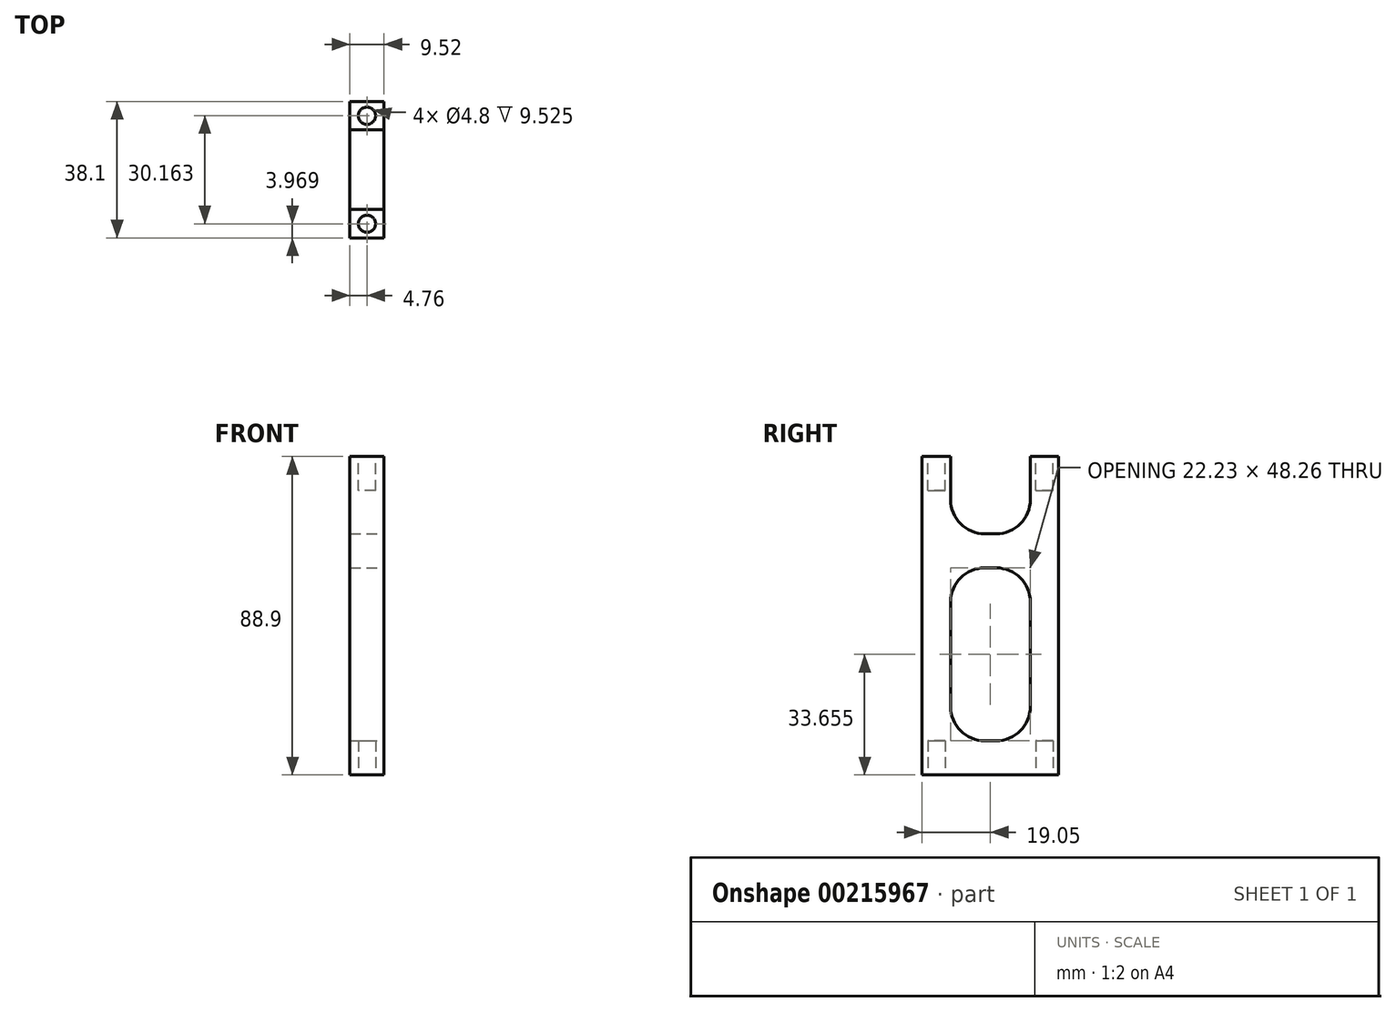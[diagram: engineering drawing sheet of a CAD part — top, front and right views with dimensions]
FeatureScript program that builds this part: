
annotation { "Feature Type Name" : "Feature", "Feature Type Description" : "" }
export const myFeature = defineFeature(function(context is Context, id is Id, definition is map)
    precondition{}
    {
        {
            var Q0;
            Q0=qCreatedBy(makeId("Right.planeOp"),FACE);
            var sketch = newSketch(context, id + "F0", { "sketchPlane" : qUnion([Q0])});
            skLineSegment(sketch, "E0.bottom", {"start": v(0, 0) * mm, "end": v(38.1, 0) * mm});
            skLineSegment(sketch, "E0.top", {"start": v(0, 88.9) * mm, "end": v(38.1, 88.9) * mm});
            skLineSegment(sketch, "E0.left", {"start": v(0, 0) * mm, "end": v(0, 88.9) * mm});
            skLineSegment(sketch, "E0.right", {"start": v(38.1, 0) * mm, "end": v(38.1, 88.9) * mm});
            skSolve(sketch);
        }
        {
            var Q0;
            Q0=qSketchRegion(id+"F0",true);
            extrude(context, id + "F1", {"entities" : qUnion([Q0]), "depth" : 9.52 * mm, "symmetric" : true});
        }
        {
            var Q0;
            Q0=makeQuery(id+"F1.opExtrude","CAP_FACE",FACE,{"disambiguationData":[OSD([sQuery(id+"F0.wireOp",EDGE,"E0.bottom"),sQuery(id+"F0.wireOp",EDGE,"E0.top"),sQuery(id+"F0.wireOp",EDGE,"E0.left"),sQuery(id+"F0.wireOp",EDGE,"E0.right")])],"isStart":false});
            var sketch = newSketch(context, id + "F2", { "sketchPlane" : qUnion([Q0])});
            skLineSegment(sketch, "E1", {"start": v(19.05, 0) * mm, "end": v(19.05, 117.7) * mm, "construction": true});
            skLineSegment(sketch, "E2", {"start": v(7.94, 88.9) * mm, "end": v(30.16, 88.9) * mm});
            skPoint(sketch, "E3", {"position": v(19.05, 88.9) * mm});
            skLineSegment(sketch, "E4", {"start": v(7.94, 88.9) * mm, "end": v(7.94, 76.84) * mm});
            skLineSegment(sketch, "E5", {"start": v(17.46, 67.31) * mm, "end": v(20.64, 67.31) * mm});
            skLineSegment(sketch, "E6", {"start": v(30.16, 88.9) * mm, "end": v(30.16, 76.84) * mm});
            skPoint(sketch, "E7.visualSharp", {"position": v(7.94, 67.31) * mm});
            skArc(sketch, "E7.filletArc", {"start": v(7.94, 76.84) * mm, "mid": v(10.73, 70.1) * mm, "end": v(17.46, 67.31) * mm});
            skPoint(sketch, "E8.visualSharp", {"position": v(30.16, 67.31) * mm});
            skArc(sketch, "E8.filletArc", {"start": v(20.64, 67.31) * mm, "mid": v(27.37, 70.1) * mm, "end": v(30.16, 76.84) * mm});
            skSolve(sketch);
        }
        {
            var Q0;
            Q0=qSketchRegion(id+"F2",true);
            extrude(context, id + "F3", {"entities" : qUnion([Q0]), "operationType" : NewBodyOperationType.REMOVE, "oppositeDirection" : true, "depth" : 25.4 * mm, "symmetric" : true});
        }
        {
            var Q0;
            {var subQ1=sQuery(id+"F0.wireOp",EDGE,"E0.left");var subQ2=sQuery(id+"F0.wireOp",EDGE,"E0.top");Q0=makeQuery(id+"F3.boolean.opBoolean","SPLIT",FACE,{"disambiguationData":[TD([makeQuery(id+"F1.opExtrude","SWEPT_FACE",FACE,{"disambiguationData":[OSD([subQ1])]})])],"derivedFrom":makeQuery(id+"F1.opExtrude","SWEPT_FACE",FACE,{"disambiguationData":[OSD([subQ2])]})});}
            var sketch = newSketch(context, id + "F4", { "sketchPlane" : qUnion([Q0])});
            skCircle(sketch, "E9", {"center": v(0, 3.97) * mm, "radius": 2.4 * mm});
            skCircle(sketch, "E10", {"center": v(0, 34.13) * mm, "radius": 2.4 * mm});
            skSolve(sketch);
        }
        {
            var Q0;
            Q0=qSketchRegion(id+"F4",true);
            extrude(context, id + "F5", {"entities" : qUnion([Q0]), "operationType" : NewBodyOperationType.REMOVE, "oppositeDirection" : true, "depth" : 9.52 * mm});
        }
        {
            var Q0;
            Q0=makeQuery(id+"F1.opExtrude","SWEPT_FACE",FACE,{"disambiguationData":[OSD([sQuery(id+"F0.wireOp",EDGE,"E0.bottom")])]});
            var sketch = newSketch(context, id + "F6", { "sketchPlane" : qUnion([Q0])});
            skCircle(sketch, "E11.0", {"center": v(0, -3.97) * mm, "radius": 2.4 * mm});
            skCircle(sketch, "E12.0", {"center": v(0, -34.13) * mm, "radius": 2.4 * mm});
            skSolve(sketch);
        }
        {
            var Q0;
            Q0=qSketchRegion(id+"F6",true);
            extrude(context, id + "F7", {"entities" : qUnion([Q0]), "operationType" : NewBodyOperationType.REMOVE, "oppositeDirection" : true, "depth" : 9.52 * mm});
        }
        {
            var Q0;
            Q0=makeQuery(id+"F1.opExtrude","CAP_FACE",FACE,{"disambiguationData":[OSD([sQuery(id+"F0.wireOp",EDGE,"E0.bottom"),sQuery(id+"F0.wireOp",EDGE,"E0.top"),sQuery(id+"F0.wireOp",EDGE,"E0.left"),sQuery(id+"F0.wireOp",EDGE,"E0.right")])],"isStart":false});
            var sketch = newSketch(context, id + "F8", { "sketchPlane" : qUnion([Q0])});
            skLineSegment(sketch, "E13", {"start": v(7.94, 76.84) * mm, "end": v(7.94, 0) * mm, "construction": true});
            skLineSegment(sketch, "E14", {"start": v(30.16, 76.84) * mm, "end": v(30.16, 0) * mm, "construction": true});
            skLineSegment(sketch, "E15.bottom", {"start": v(7.94, 57.79) * mm, "end": v(30.16, 57.79) * mm});
            skLineSegment(sketch, "E15.top", {"start": v(7.94, 9.53) * mm, "end": v(30.16, 9.53) * mm});
            skLineSegment(sketch, "E15.left", {"start": v(7.94, 57.79) * mm, "end": v(7.94, 9.52) * mm});
            skLineSegment(sketch, "E15.right", {"start": v(30.16, 57.79) * mm, "end": v(30.16, 9.52) * mm});
            skSolve(sketch);
        }
        {
            var Q0;
            Q0=qSketchRegion(id+"F8",true);
            extrude(context, id + "F9", {"entities" : qUnion([Q0]), "operationType" : NewBodyOperationType.REMOVE, "endBound" : BoundingType.THROUGH_ALL, "oppositeDirection" : true, "depth" : 25.4 * mm});
        }
        {
            var Q0;
            Q0=makeQuery(id+"F9.boolean.opBoolean","COPY",EDGE,{"derivedFrom":makeQuery(id+"F9.opExtrude","SWEPT_EDGE",EDGE,{"disambiguationData":[OSD([sQuery(id+"F8.wireOp",EDGE,"E15.bottom"),sQuery(id+"F8.wireOp",EDGE,"E15.left")])]})});
            var Q1;
            Q1=makeQuery(id+"F9.boolean.opBoolean","COPY",EDGE,{"derivedFrom":makeQuery(id+"F9.opExtrude","SWEPT_EDGE",EDGE,{"disambiguationData":[OSD([sQuery(id+"F8.wireOp",EDGE,"E15.bottom"),sQuery(id+"F8.wireOp",EDGE,"E15.right")])]})});
            var Q2;
            Q2=makeQuery(id+"F9.boolean.opBoolean","COPY",EDGE,{"derivedFrom":makeQuery(id+"F9.opExtrude","SWEPT_EDGE",EDGE,{"disambiguationData":[OSD([sQuery(id+"F8.wireOp",EDGE,"E15.top"),sQuery(id+"F8.wireOp",EDGE,"E15.left")])]})});
            var Q3;
            Q3=makeQuery(id+"F9.boolean.opBoolean","COPY",EDGE,{"derivedFrom":makeQuery(id+"F9.opExtrude","SWEPT_EDGE",EDGE,{"disambiguationData":[OSD([sQuery(id+"F8.wireOp",EDGE,"E15.top"),sQuery(id+"F8.wireOp",EDGE,"E15.right")])]})});
            fillet(context, id + "F10", {"entities" : qUnion([Q0, Q1, Q2, Q3]), "radius" : 9.52 * mm, "tangentPropagation" : true, "allowEdgeOverflow" : false});
        }
    });
